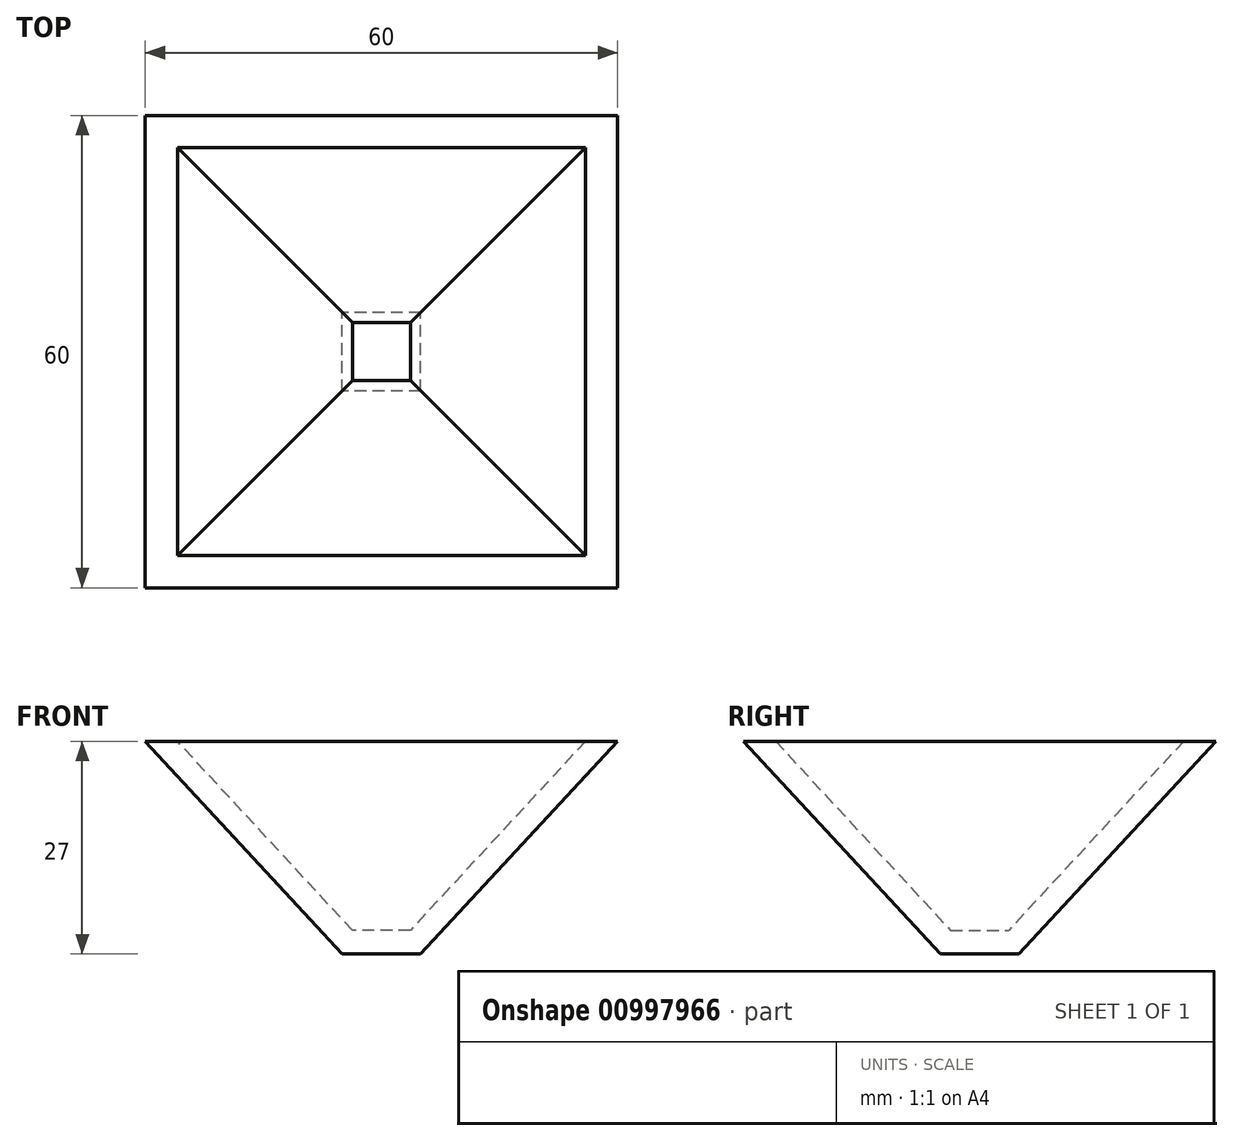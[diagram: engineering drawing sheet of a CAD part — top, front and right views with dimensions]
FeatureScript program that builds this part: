
annotation { "Feature Type Name" : "Feature", "Feature Type Description" : "" }
export const myFeature = defineFeature(function(context is Context, id is Id, definition is map)
    precondition{}
    {
        {
            var Q0;
            Q0=qCreatedBy(makeId("Top.planeOp"),FACE);
            var sketch = newSketch(context, id + "F0", { "sketchPlane" : qUnion([Q0])});
            skLineSegment(sketch, "E0.bottom", {"start": v(5, -5) * mm, "end": v(-5, -5) * mm});
            skLineSegment(sketch, "E0.top", {"start": v(5, 5) * mm, "end": v(-5, 5) * mm});
            skLineSegment(sketch, "E0.left", {"start": v(5, -5) * mm, "end": v(5, 5) * mm});
            skLineSegment(sketch, "E0.right", {"start": v(-5, -5) * mm, "end": v(-5, 5) * mm});
            skPoint(sketch, "E0.middle", {"position": v(0, 0) * mm});
            skSolve(sketch);
        }
        {
            var Q0;
            Q0=qCreatedBy(makeId("Top.planeOp"),FACE);
            cPlane(context, id + "F1", {"entities" : qUnion([Q0]), "cplaneType" : CPlaneType.OFFSET, "offset" : 27 * mm, "width" : 150 * mm, "height" : 150 * mm});
        }
        {
            var Q0;
            Q0=qCreatedBy(id+"F1.planeOp",FACE);
            var sketch = newSketch(context, id + "F2", { "sketchPlane" : qUnion([Q0])});
            skLineSegment(sketch, "E1.bottom", {"start": v(30, -30) * mm, "end": v(-30, -30) * mm});
            skLineSegment(sketch, "E1.top", {"start": v(30, 30) * mm, "end": v(-30, 30) * mm});
            skLineSegment(sketch, "E1.left", {"start": v(30, -30) * mm, "end": v(30, 30) * mm});
            skLineSegment(sketch, "E1.right", {"start": v(-30, -30) * mm, "end": v(-30, 30) * mm});
            skPoint(sketch, "E1.middle", {"position": v(0, 0) * mm});
            skSolve(sketch);
        }
        {
            var Q0;
            Q0=makeQuery(id+"F0.imprint","IMPRINT",FACE,{"disambiguationData":[TD([[makeQuery(id+"F0.imprint","IMPRINT",EDGE,{"derivedFrom":sQuery(id+"F0.wireOp",EDGE,"E0.bottom")}),-1.0]])]});
            var Q1;
            Q1=makeQuery(id+"F2.imprint","IMPRINT",FACE,{"disambiguationData":[TD([[makeQuery(id+"F2.imprint","IMPRINT",EDGE,{"derivedFrom":sQuery(id+"F2.wireOp",EDGE,"E1.bottom")}),-1.0]])]});
            loft(context, id + "F3", {"sheetProfilesArray" : [{ "sheetProfileEntities" : qUnion([Q0]) }, { "sheetProfileEntities" : qUnion([Q1]) }]});
        }
        {
            var Q0;
            Q0=makeQuery(id+"F3.opLoft","CAP_FACE",FACE,{"disambiguationData":[OSD([makeQuery(id+"F2.imprint","IMPRINT",FACE,{"disambiguationData":[TD([[makeQuery(id+"F2.imprint","IMPRINT",EDGE,{"derivedFrom":sQuery(id+"F2.wireOp",EDGE,"E1.bottom")}),-1.0]])]})])],"isStart":true});
            var Q1;
            Q1=makeQuery(id+"F3.opLoft","SWEPT_BODY",BODY,{"disambiguationData":[OSD([makeQuery(id+"F0.imprint","IMPRINT",FACE,{"disambiguationData":[TD([[makeQuery(id+"F0.imprint","IMPRINT",EDGE,{"derivedFrom":sQuery(id+"F0.wireOp",EDGE,"E0.bottom")}),-1.0]])]}),makeQuery(id+"F2.imprint","IMPRINT",FACE,{"disambiguationData":[TD([[makeQuery(id+"F2.imprint","IMPRINT",EDGE,{"derivedFrom":sQuery(id+"F2.wireOp",EDGE,"E1.bottom")}),-1.0]])]})])]});
            shell(context, id + "F4", {"entities" : qUnion([Q0]), "parts" : qUnion([Q1]), "thickness" : 3 * mm});
        }
    });
